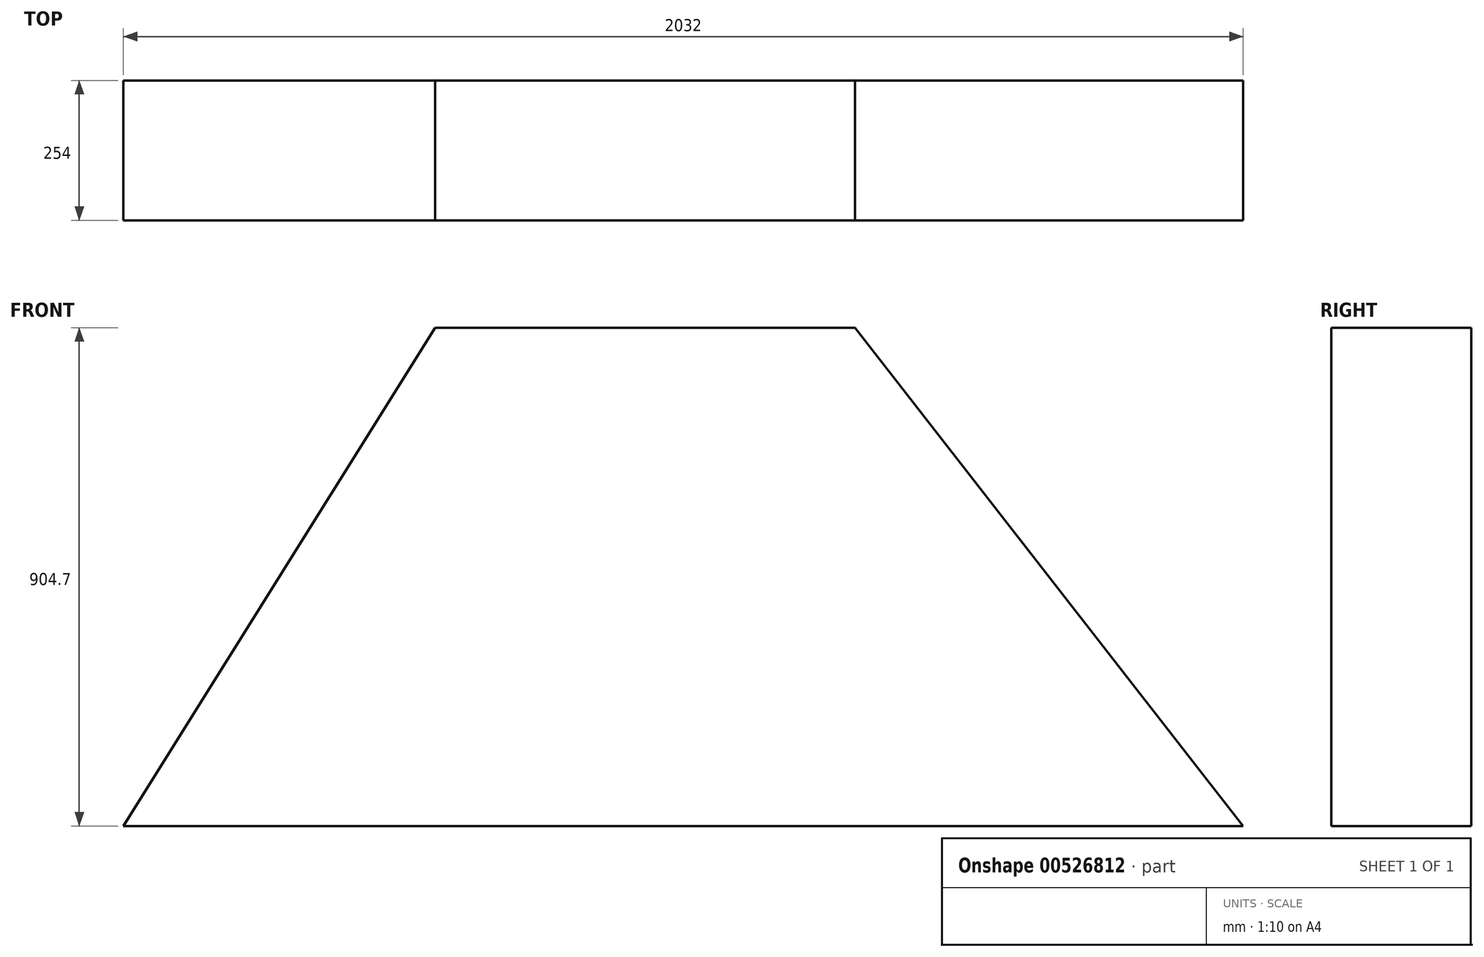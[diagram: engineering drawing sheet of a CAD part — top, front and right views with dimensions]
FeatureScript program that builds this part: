
annotation { "Feature Type Name" : "Feature", "Feature Type Description" : "" }
export const myFeature = defineFeature(function(context is Context, id is Id, definition is map)
    precondition{}
    {
        {
            var Q0;
            Q0=qCreatedBy(makeId("Front.planeOp"),FACE);
            var sketch = newSketch(context, id + "F0", { "sketchPlane" : qUnion([Q0])});
            skLineSegment(sketch, "E0", {"start": v(-116.88, -48.53) * mm, "end": v(1915.12, -48.53) * mm});
            skLineSegment(sketch, "E1", {"start": v(1915.12, -48.53) * mm, "end": v(1210.44, 856.17) * mm});
            skLineSegment(sketch, "E2", {"start": v(1210.44, 856.17) * mm, "end": v(448.44, 856.17) * mm});
            skLineSegment(sketch, "E3", {"start": v(448.44, 856.17) * mm, "end": v(-116.88, -48.53) * mm});
            skSolve(sketch);
        }
        {
            var Q0;
            Q0=makeQuery(id+"F0.imprint","IMPRINT",FACE,{"disambiguationData":[TD([[makeQuery(id+"F0.imprint","IMPRINT",EDGE,{"derivedFrom":sQuery(id+"F0.wireOp",EDGE,"E0")}),1.0]])]});
            extrude(context, id + "F1", {"entities" : qUnion([Q0]), "depth" : 254 * mm, "offsetDistance" : 25.4 * mm});
        }
    });
